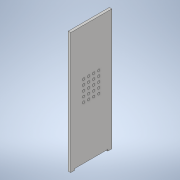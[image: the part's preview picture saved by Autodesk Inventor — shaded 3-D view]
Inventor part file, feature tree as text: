
AUTODESK INVENTOR PART (.ipt)
format: ipt  version: 2020 (Build 240168000, 168)  size: 142,336 bytes
history: native  units: mm
features: sketch x2, extrude x1
ambient origin geometry x8: Origin, YZ Plane, XZ Plane, XY Plane, X Axis, Y Axis, Z Axis, Center Point
bodies: Solid1 (feature_tree)
feature tree (3):
  sketch  "Sketch1"  dims[d0=241.0mm d1=82.0mm]
  sketch  "Sketch2"  dims[d2=38.0mm d3=41.0mm d4=174.0mm d5=66.0mm d6=3.0mm d7=8.0mm d21=4.7mm d22=50.0mm d24=10.0mm d25=40.0mm d27=10.0mm d32=5.0mm d33=0.0mm]
  extrude  "Extrusion1"  Depth=82.0mm
